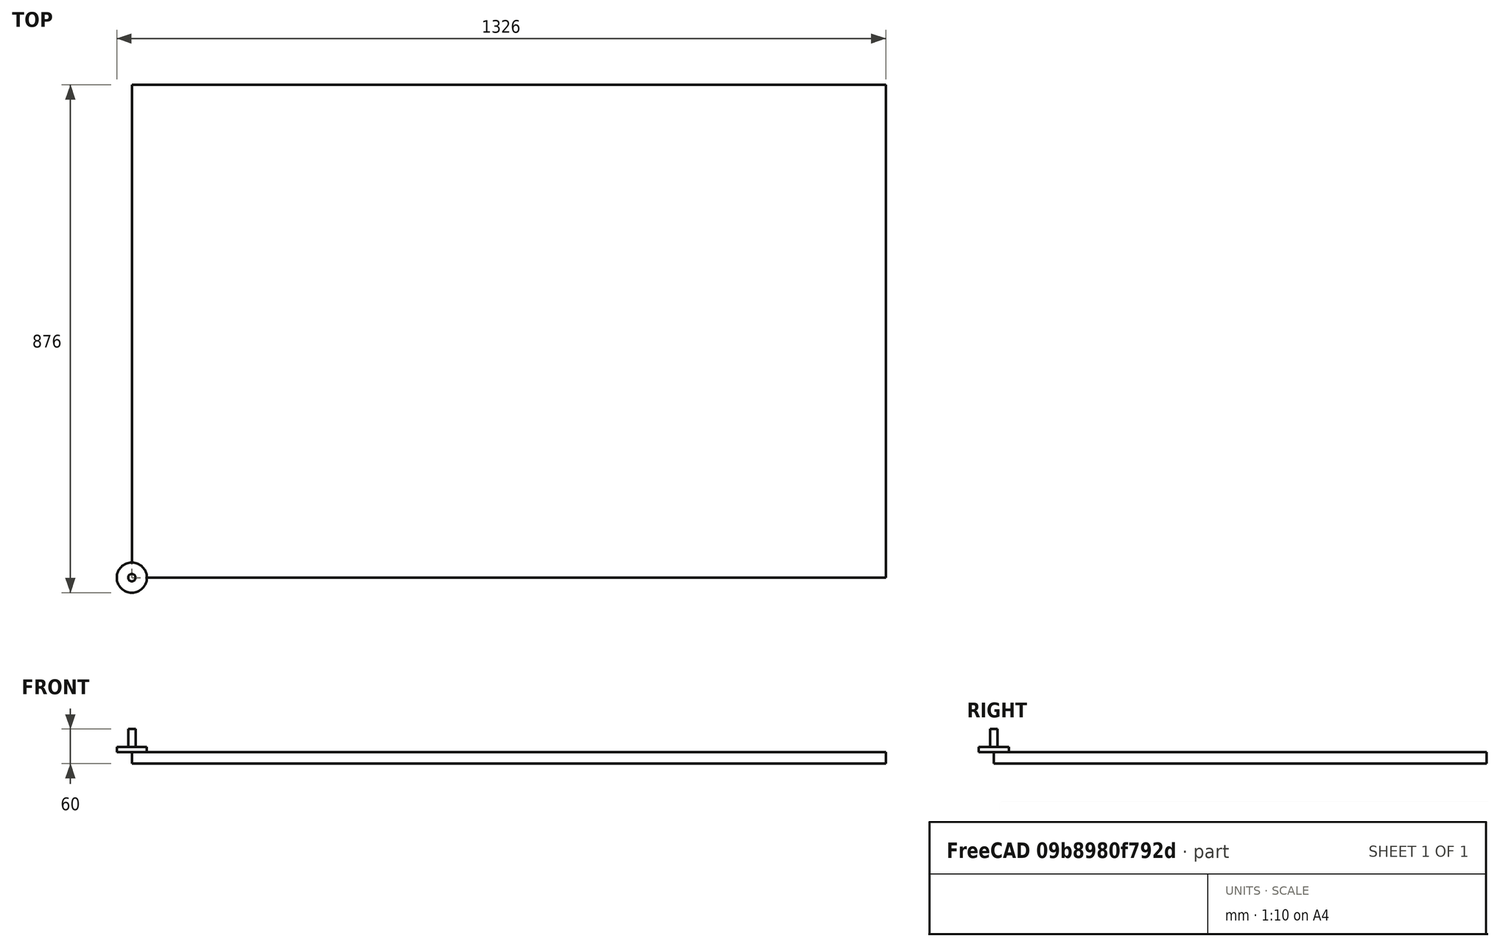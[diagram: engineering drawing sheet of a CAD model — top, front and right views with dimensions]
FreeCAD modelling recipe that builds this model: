
FCSTD DOCUMENT  (FreeCAD 0.19R14555 (Git shallow))
Label: PineTable
License: All rights reserved
LicenseURL: http://en.wikipedia.org/wiki/All_rights_reserved
objects: Part::FeaturePython×4, Path::FeaturePython×3, Mesh::FeaturePython×3, Sketcher::SketchObject×2, PartDesign::Body×2, App::FeaturePython×2, App::DocumentObjectGroup×2, PartDesign::Pad×1, Path::FeatureCompoundPython×1, PartDesign::Revolution×1
note: 13 computed .brp shape members not serialized (recipe doc carries the construction recipe); baked Part::Feature solids carry a one-line shape summary decoded from their .brp

FEATURE [Sketcher::SketchObject] Sketch
  FullyConstrained = true
  MapMode = 5
  Support = -> [XY_Plane]
  sketch-geometry (4):
    g0: LineSegment StartX=0 StartY=850 StartZ=0 EndX=1300 EndY=850 EndZ=0
    g1: LineSegment StartX=1300 StartY=850 StartZ=0 EndX=1300 EndY=0 EndZ=0
    g2: LineSegment StartX=1300 StartY=0 StartZ=0 EndX=0 EndY=0 EndZ=0
    g3: LineSegment StartX=0 StartY=0 StartZ=0 EndX=0 EndY=850 EndZ=0
  constraints (11):
    c: Coincident(g0,g1)
    c: Coincident(g1,g2)
    c: Coincident(g2,g3)
    c: Coincident(g3,g0)
    c: Horizontal(g0)
    c: Horizontal(g2)
    c: Vertical(g1)
    c: Vertical(g3)
    c: Coincident(g2,g-1)
    c: DistanceX(g2,g2) = 1300
    c: DistanceY(g3,g3) = 850
FEATURE [PartDesign::Pad] Pad
  Direction = (1,1,1)
  Length = 20
  Length2 = 100
  Profile = -> Sketch
  Reversed = true
  Type = 0
FEATURE [PartDesign::Body] Body
  Group = -> [Sketch,Pad]
  Origin = -> Origin
  Tip = -> Pad
FEATURE [App::FeaturePython] SetupSheet  # Path/CAM operation (typed FeaturePython)
  ClearanceHeightExpression = OpStockZMax+SetupSheet.ClearanceHeightOffset
  ClearanceHeightOffset = 5
  CoolantMode = 0
  CoolantModes = None | Flood | Mist
  FinalDepthExpression = OpFinalDepth
  HorizRapid = 0
  SafeHeightExpression = OpStockZMax+SetupSheet.SafeHeightOffset
  SafeHeightOffset = 3
  StartDepthExpression = OpStartDepth
  StepDownExpression = OpToolDiameter
  VertRapid = 0
FEATURE [Part::FeaturePython] Clone  label="Model-Body"  # Draft clone (typed FeaturePython)
  AttacherType = Attacher::AttachEngine3D
  Fuse = false
  Objects = -> [Body]
  PathResource = Model
  Scale = (1,1,1)
FEATURE [App::DocumentObjectGroup] Model
  Group = -> [Clone]
FEATURE [Part::FeaturePython] ToolBit001  label="52mm Endmill"  # Path/CAM toolbit (typed FeaturePython)
  BitPropertyNames = Chipload | CuttingEdgeHeight | Diameter | Flutes | Length | Material | ShankDiameter
  BitShape = /app/freecad/Mod/Path/Tools/Shape/endmill.fcstd
  Chipload = 0
  CuttingEdgeHeight = 9
  Diameter = 52
  File = <userpath>/Documents/MensShed/FreeCAD/Bit/52mm_EndMill.fctb
  Flutes = 0
  Length = 40
  Material = 0
  ShankDiameter = 12.7
  ShapeName = endmill
FEATURE [Path::FeaturePython] _2mm_Endmill  label="52mm Endmill001"  # Path/CAM operation (typed FeaturePython)
  HorizFeed = 40
  HorizRapid = 0
  SpindleDir = 0
  SpindleSpeed = 10000
  Tool = -> ToolBit001
  ToolNumber = 1
  VertFeed = 40
  VertRapid = 0
  expr: VertRapid = SetupSheet.VertRapid
  expr: HorizRapid = SetupSheet.HorizRapid
FEATURE [App::DocumentObjectGroup] Tools
  Group = -> [_2mm_Endmill]
FEATURE [Path::FeaturePython] MillFace  # Path/CAM operation (typed FeaturePython)
  Active = true
  AreaParams:
    Tolerance = 1e-07
    FitArcs = True
    Simplify = False
    CleanDistance = 0.0
    Accuracy = 0.01
    Unit = 1.0
    MinArcPoints = 4
    MaxArcPoints = 100
    ClipperScale = 10000000.0
    Fill = 0
    Coplanar = 0
    Reorient = True
    Outline = False
    Explode = False
    OpenMode = 0
    Deflection = 0.01
    SubjectFill = 0
    ClipFill = 0
    Offset = 0.0
    ExtraPass = 0
    Stepover = 0.0
    LastStepover = 0.0
    JoinType = 0
    EndType = 0
    MiterLimit = 2.0
    RoundPrecision = 0.0
    PocketMode = 1
    ToolRadius = 26.0
    PocketExtraOffset = 0.0
    PocketStepover = 26.0
    PocketLastStepover = 0.0
    FromCenter = True
    Angle = 0.0
    AngleShift = 0.0
    Shift = 0.0
    Thicken = False
    SectionCount = -1
    Stepdown = 1.0
    SectionOffset = 0.0
    SectionTolerance = 1e-06
    SectionMode = 2
    Project = False
  Base = -> [Clone]
  BoundaryShape = 0
  ClearEdges = true
  ClearanceHeight = 5
  CoolantMode = Mist
  CutMode = 1
  CycleTime = 00:37:55
  EnableRotation = 0
  ExcludeRaisedAreas = false
  ExtraOffset = 0
  FinalDepth = -5
  FinishDepth = 2
  KeepToolDown = false
  MinTravel = false
  OffsetPattern = 0
  OpFinalDepth = 0
  OpStartDepth = 3
  OpStockZMax = 0
  OpStockZMin = -20
  OpToolDiameter = 52
  PathParams = {'orientation': 0, 'feedrate': 40.0, 'feedrate_v': 40.0, 'verbose': True, 'resume_height': 3.0, 'retraction': 5.0, 'return_end': True, 'preamble': False}
  SafeHeight = 3
  StartAt = 0
  StartDepth = 0
  StartPoint = (0,0,0)
  StepDown = 3
  StepOver = 50
  ToolController = -> _2mm_Endmill
  UseStartPoint = false
  ZigZagAngle = 0
  expr: StartDepth = 0
  expr: FinalDepth = -5mm
  expr: SafeHeight = OpStockZMax + SetupSheet.SafeHeightOffset
  expr: ClearanceHeight = OpStockZMax + SetupSheet.ClearanceHeightOffset
  expr: StepDown = 3mm
  expr: FinishDepth = 2mm
FEATURE [Path::FeatureCompoundPython] Operations  # Path/CAM operation (typed FeaturePython)
  Group = -> [MillFace]
  UsePlacements = false
FEATURE [Mesh::FeaturePython] CutMaterial  # WARN: FeaturePython — macro-defined, semantics opaque (R4)
FEATURE [Sketcher::SketchObject] Sketch001
  FullyConstrained = true
  MapMode = 5
  Placement = pos=(0,0,0) rot=(1,0,0;1.5708rad)
  Support = -> [XZ_Plane001]
  expr: Constraints[18] = <<Attributes>>.CuttingEdgeHeight
  expr: Constraints[16] = <<Attributes>>.ShankDiameter
  expr: Constraints[10] = <<Attributes>>.Length
  expr: Constraints[9] = <<Attributes>>.Diameter
  sketch-geometry (8):
    g0: LineSegment StartX=0 StartY=40 StartZ=0 EndX=0 EndY=0 EndZ=0
    g1: LineSegment StartX=0 StartY=0 StartZ=0 EndX=26 EndY=0 EndZ=0
    g2: LineSegment StartX=26 StartY=0 StartZ=0 EndX=26 EndY=9 EndZ=0
    g3: LineSegment StartX=6.35 StartY=40 StartZ=0 EndX=0 EndY=40 EndZ=0
    g4: LineSegment StartX=26 StartY=0 StartZ=0 EndX=-26 EndY=0 EndZ=0
    g5: LineSegment StartX=6.35 StartY=8.99 StartZ=0 EndX=26 EndY=9 EndZ=0
    g6: LineSegment StartX=6.35 StartY=40 StartZ=0 EndX=6.35 EndY=8.99 EndZ=0
    g7: LineSegment StartX=-6.35 StartY=40 StartZ=0 EndX=6.35 EndY=40 EndZ=0
  constraints (21):
    c: Vertical(g0)
    c: Coincident(g0,g1)
    c: Horizontal(g1)
    c: Coincident(g1,g2)
    c: Vertical(g2)
    c: Horizontal(g3)
    c: Coincident(g0,g3)
    c: Coincident(g4,g1)
    c: Symmetric(g1,g4,g0)
    c: DistanceX(g4,g4) = 52
    c: DistanceY(g2,g3) = 40
    c: Coincident(g2,g5)
    c: Vertical(g6)
    c: Coincident(g3,g6)
    c: Symmetric(g7,g7,g0)
    c: Coincident(g7,g3)
    c: DistanceX(g7,g7) = 12.7
    c: Coincident(g5,g6)
    c: DistanceY(g2) = 9
    c: Coincident(g0,g-1)
    c: DistanceY(g5,g2) = 0.01
FEATURE [PartDesign::Revolution] Revolution
  AllowMultiFace = false
  Angle = 360
  Axis = (0,-2e-16,1)
  Base = (0,0,0)
  Placement = pos=(0,0,0) rot=(1,0,0;1.5708rad)
  Profile = -> Sketch001
  ReferenceAxis = -> Sketch001 [V_Axis]
  Reversed = true
FEATURE [App::FeaturePython] PropertyBag  label="Attributes"  # WARN: FeaturePython — macro-defined, semantics opaque (R4)
  Chipload = 0
  CustomPropertyGroups = Attributes | Shape
  CuttingEdgeHeight = 9
  Diameter = 52
  Flutes = 0
  Length = 40
  Material = 0
  ShankDiameter = 12.7
FEATURE [PartDesign::Body] Body001  label="Endmill001"
  Group = -> [Sketch001,Revolution,PropertyBag]
  Origin = -> Origin001
  Tip = -> Revolution
FEATURE [Part::FeaturePython] ToolBit  label="52mm Endmill002"  # Path/CAM toolbit (typed FeaturePython)
  BitBody = -> Body001
  BitPropertyNames = Chipload | CuttingEdgeHeight | Diameter | Flutes | Length | Material | ShankDiameter
  BitShape = /app/freecad/Mod/Path/Tools/Shape/endmill.fcstd
  Chipload = 0
  CuttingEdgeHeight = 9
  Diameter = 52
  Flutes = 0
  Length = 40
  Material = 0
  ShankDiameter = 12.7
  ShapeName = endmill
FEATURE [Mesh::FeaturePython] CutMaterial001  # WARN: FeaturePython — macro-defined, semantics opaque (R4)
FEATURE [Part::FeaturePython] Stock  # WARN: FeaturePython — macro-defined, semantics opaque (R4)
  Height = 20
  Length = 1300
  Placement = pos=(0,0,-20) rot=(0,0,1;0rad)
  StockType = CreateBox
  Width = 850
FEATURE [Path::FeaturePython] Job  # Path/CAM operation (typed FeaturePython)
  CycleTime = 00:37:55
  Fixtures = G54
  GeometryTolerance = 0.01
  LastPostProcessDate = 2022-01-27 09:04:34.072546
  LastPostProcessOutput = <userpath>/Documents/MensShed/PineTable.ngc
  Model = -> Model
  Operations = -> Operations
  OrderOutputBy = 0
  PostProcessor = 7
  PostProcessorOutputFile = <userpath>/Documents/MensShed/PineTable.ngc
  SetupSheet = -> SetupSheet
  SplitOutput = false
  Stock = -> Stock
  Tools = -> Tools
FEATURE [Mesh::FeaturePython] CutMaterial002  # WARN: FeaturePython — macro-defined, semantics opaque (R4)
